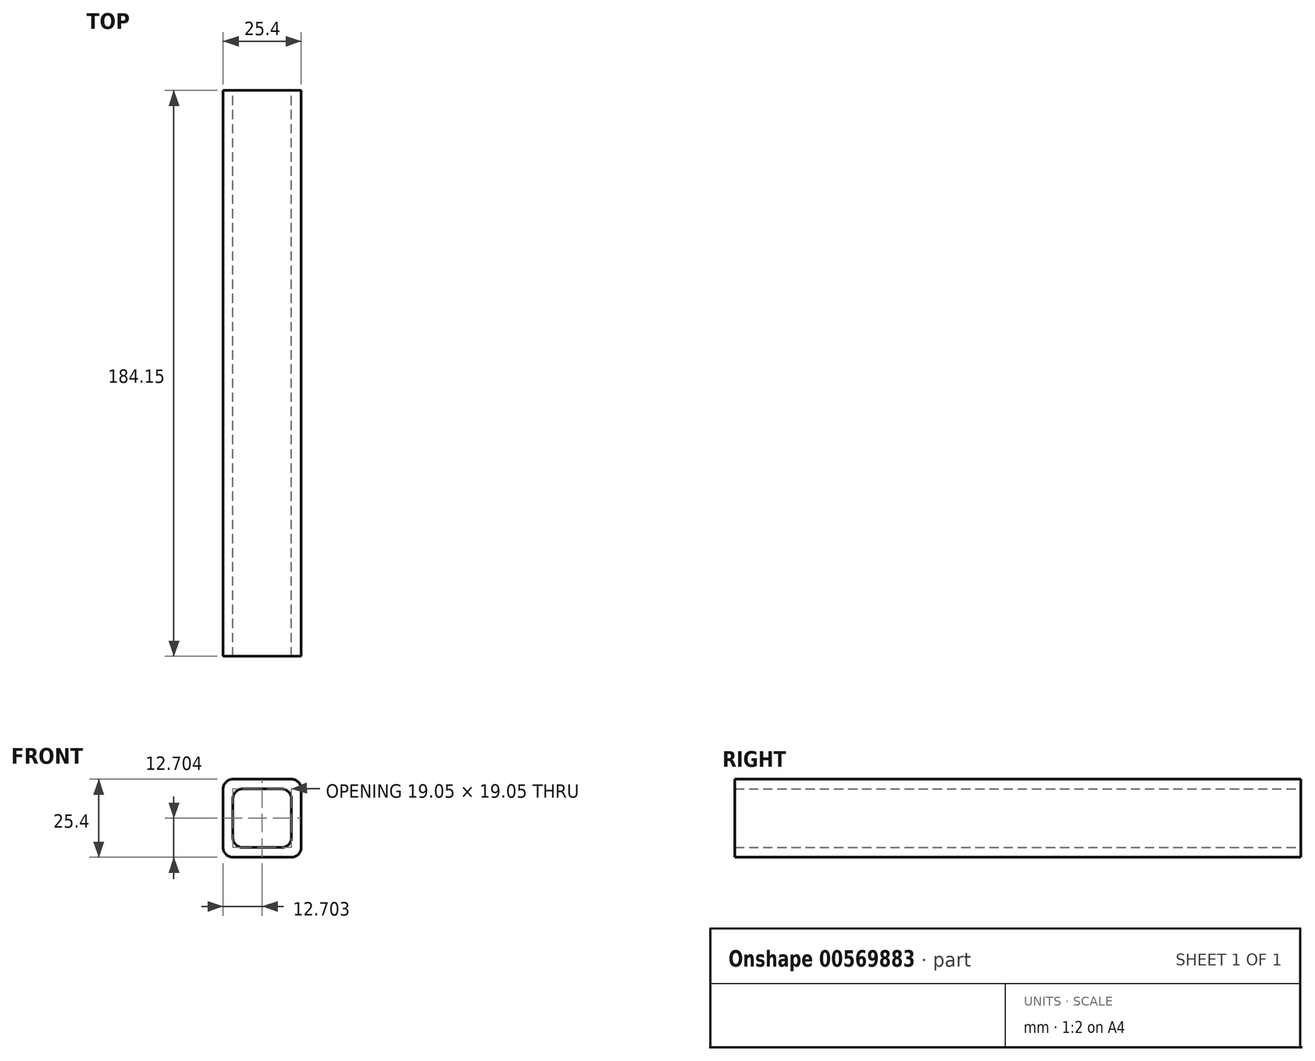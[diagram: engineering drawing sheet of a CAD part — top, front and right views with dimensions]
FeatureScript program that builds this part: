
annotation { "Feature Type Name" : "Feature", "Feature Type Description" : "" }
export const myFeature = defineFeature(function(context is Context, id is Id, definition is map)
    precondition{}
    {
        {
            var Q0;
            Q0=qCreatedBy(makeId("Front.planeOp"),FACE);
            var sketch = newSketch(context, id + "F0", { "sketchPlane" : qUnion([Q0])});
            skLineSegment(sketch, "E0.bottom", {"start": v(8.96, -12.6) * mm, "end": v(-10.1, -12.6) * mm});
            skLineSegment(sketch, "E0.top", {"start": v(8.96, 12.8) * mm, "end": v(-10.1, 12.8) * mm});
            skLineSegment(sketch, "E0.left", {"start": v(12.13, -9.43) * mm, "end": v(12.13, 9.62) * mm});
            skLineSegment(sketch, "E0.right", {"start": v(-13.27, -9.43) * mm, "end": v(-13.27, 9.62) * mm});
            skLineSegment(sketch, "E1.bottom", {"start": v(5.78, -9.43) * mm, "end": v(-6.92, -9.43) * mm});
            skLineSegment(sketch, "E1.top", {"start": v(5.78, 9.62) * mm, "end": v(-6.92, 9.62) * mm});
            skLineSegment(sketch, "E1.left", {"start": v(8.96, -6.26) * mm, "end": v(8.96, 6.44) * mm});
            skLineSegment(sketch, "E1.right", {"start": v(-10.1, -6.26) * mm, "end": v(-10.1, 6.44) * mm});
            skPoint(sketch, "E2.visualSharp", {"position": v(8.96, 9.62) * mm});
            skArc(sketch, "E2.filletArc", {"start": v(8.96, 6.44) * mm, "mid": v(8.03, 8.69) * mm, "end": v(5.78, 9.62) * mm});
            skPoint(sketch, "E3.visualSharp", {"position": v(-10.1, 9.62) * mm});
            skArc(sketch, "E3.filletArc", {"start": v(-6.92, 9.62) * mm, "mid": v(-9.16, 8.69) * mm, "end": v(-10.1, 6.44) * mm});
            skPoint(sketch, "E4.visualSharp", {"position": v(-10.1, -9.43) * mm});
            skArc(sketch, "E4.filletArc", {"start": v(-10.1, -6.26) * mm, "mid": v(-9.16, -8.5) * mm, "end": v(-6.92, -9.43) * mm});
            skPoint(sketch, "E5.visualSharp", {"position": v(8.96, -9.43) * mm});
            skArc(sketch, "E5.filletArc", {"start": v(5.78, -9.43) * mm, "mid": v(8.03, -8.5) * mm, "end": v(8.96, -6.26) * mm});
            skPoint(sketch, "E6.visualSharp", {"position": v(12.13, 12.8) * mm});
            skArc(sketch, "E6.filletArc", {"start": v(12.13, 9.62) * mm, "mid": v(11.2, 11.86) * mm, "end": v(8.96, 12.8) * mm});
            skPoint(sketch, "E7.visualSharp", {"position": v(-13.27, 12.8) * mm});
            skArc(sketch, "E7.filletArc", {"start": v(-10.1, 12.8) * mm, "mid": v(-12.34, 11.86) * mm, "end": v(-13.27, 9.62) * mm});
            skPoint(sketch, "E8.visualSharp", {"position": v(-13.27, -12.6) * mm});
            skArc(sketch, "E8.filletArc", {"start": v(-13.27, -9.43) * mm, "mid": v(-12.34, -11.68) * mm, "end": v(-10.1, -12.6) * mm});
            skPoint(sketch, "E9.visualSharp", {"position": v(12.13, -12.6) * mm});
            skArc(sketch, "E9.filletArc", {"start": v(8.96, -12.6) * mm, "mid": v(11.2, -11.68) * mm, "end": v(12.13, -9.43) * mm});
            skSolve(sketch);
        }
        {
            var Q0;
            Q0 = qSketchRegion(id + "F0", true);
            extrude(context, id + "F1", {"entities" : qUnion([Q0]), "depth" : 184.15 * mm, "offsetDistance" : 25.4 * mm});
        }
    });
